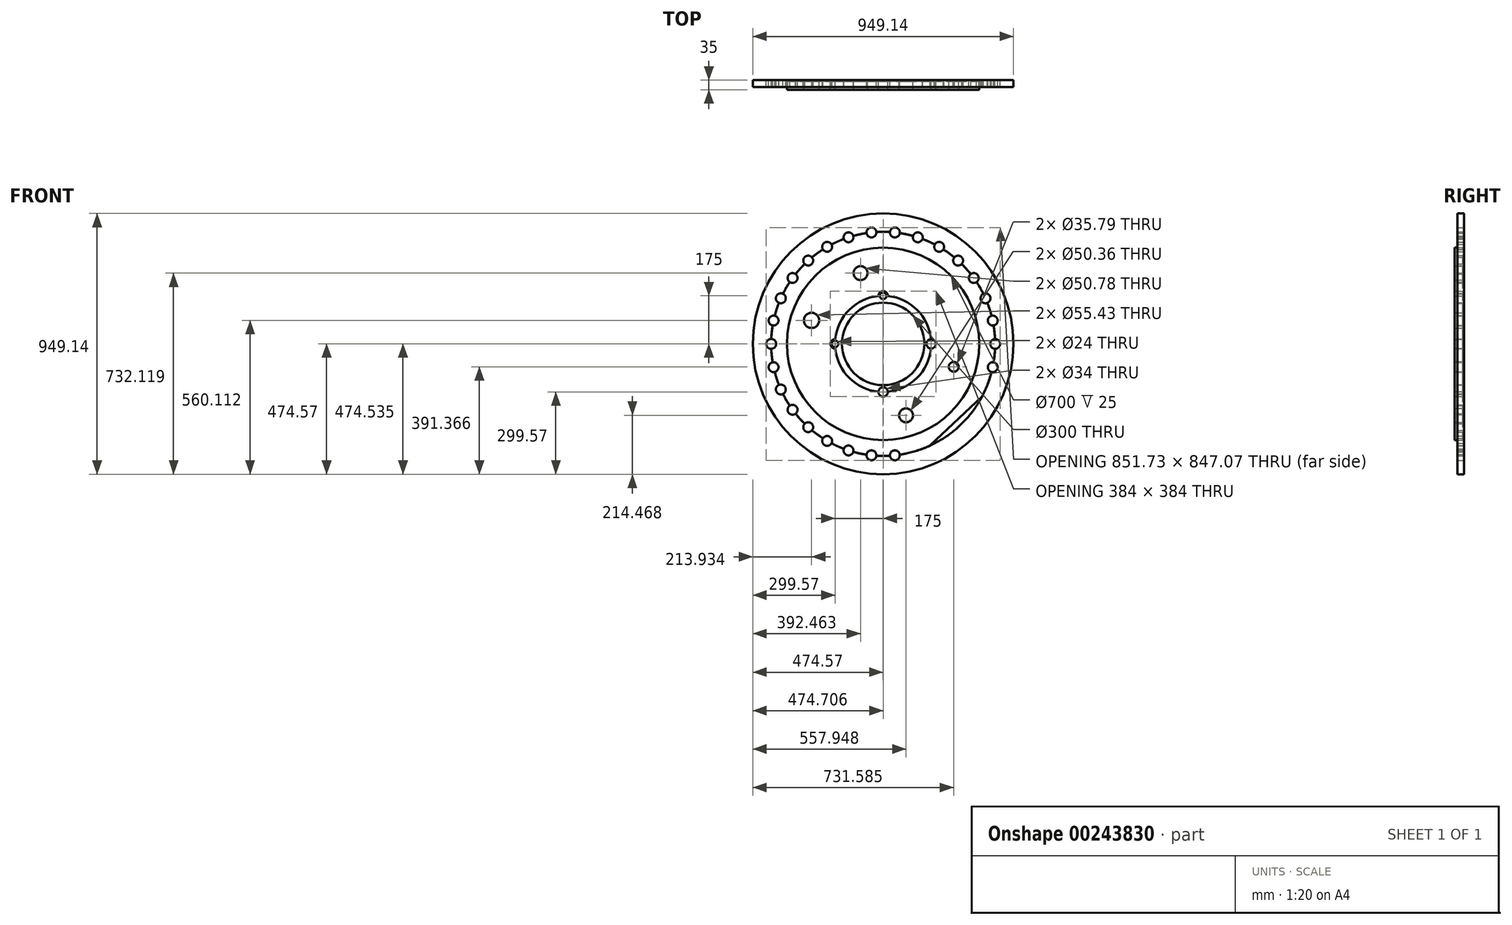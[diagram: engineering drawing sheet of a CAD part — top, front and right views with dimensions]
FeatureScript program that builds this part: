
annotation { "Feature Type Name" : "Feature", "Feature Type Description" : "" }
export const myFeature = defineFeature(function(context is Context, id is Id, definition is map)
    precondition{}
    {
        {
            var Q0;
            Q0=qCreatedBy(makeId("Front.planeOp"),FACE);
            var sketch = newSketch(context, id + "F0", { "sketchPlane" : qUnion([Q0])});
            skCircle(sketch, "E0", {"center": v(0, 0) * mm, "radius": 150 * mm});
            skCircle(sketch, "E1", {"center": v(0, 0) * mm, "radius": 175 * mm});
            skLineSegment(sketch, "E2", {"start": v(0, -200.12) * mm, "end": v(0, 224.8) * mm});
            skCircle(sketch, "E3", {"center": v(0, 175) * mm, "radius": 12 * mm});
            skCircle(sketch, "E4", {"center": v(-175, 0) * mm, "radius": 12 * mm});
            skCircle(sketch, "E5", {"center": v(175, 0) * mm, "radius": 12 * mm});
            skCircle(sketch, "E6", {"center": v(0, -175) * mm, "radius": 12 * mm});
            skCircle(sketch, "E7", {"center": v(0, 175) * mm, "radius": 17 * mm});
            skCircle(sketch, "E8", {"center": v(175, 0) * mm, "radius": 17 * mm});
            skCircle(sketch, "E9", {"center": v(0, -175) * mm, "radius": 17 * mm});
            skCircle(sketch, "E10", {"center": v(-175, 0) * mm, "radius": 17 * mm});
            skCircle(sketch, "E11", {"center": v(0, 0) * mm, "radius": 350 * mm});
            skCircle(sketch, "E12", {"center": v(0, 0) * mm, "radius": 474.57 * mm});
            skCircle(sketch, "E13", {"center": v(0, 0) * mm, "radius": 407.73 * mm});
            skCircle(sketch, "E14.1.0", {"center": v(-0.05, -0.03) * mm, "radius": 407.73 * mm});
            skCircle(sketch, "E14.2.0", {"center": v(0, -0.06) * mm, "radius": 407.73 * mm});
            skPoint(sketch, "E14.center", {"position": v(-0.02, -0.03) * mm});
            skCircle(sketch, "E15", {"center": v(-407.73, 0) * mm, "radius": 18 * mm});
            skCircle(sketch, "E16.1.0", {"center": v(-398.83, -84.8) * mm, "radius": 18 * mm});
            skCircle(sketch, "E16.1.1", {"center": v(0.01, -0.09) * mm, "radius": 407.73 * mm});
            skCircle(sketch, "E16.2.0", {"center": v(-372.48, -165.9) * mm, "radius": 18 * mm});
            skCircle(sketch, "E16.2.1", {"center": v(0.03, -0.11) * mm, "radius": 407.73 * mm});
            skCircle(sketch, "E16.3.0", {"center": v(-329.86, -239.74) * mm, "radius": 18 * mm});
            skCircle(sketch, "E16.3.1", {"center": v(0.04, -0.14) * mm, "radius": 407.73 * mm});
            skCircle(sketch, "E16.4.0", {"center": v(-272.8, -303.12) * mm, "radius": 18 * mm});
            skCircle(sketch, "E16.4.1", {"center": v(0.07, -0.15) * mm, "radius": 407.73 * mm});
            skCircle(sketch, "E16.5.0", {"center": v(-203.83, -353.24) * mm, "radius": 18 * mm});
            skCircle(sketch, "E16.5.1", {"center": v(0.1, -0.16) * mm, "radius": 407.73 * mm});
            skCircle(sketch, "E16.6.0", {"center": v(-125.94, -387.93) * mm, "radius": 18 * mm});
            skCircle(sketch, "E16.7.0", {"center": v(-42.53, -405.66) * mm, "radius": 18 * mm});
            skCircle(sketch, "E16.7.1", {"center": v(0.15, -0.17) * mm, "radius": 407.73 * mm});
            skCircle(sketch, "E16.8.0", {"center": v(42.73, -405.67) * mm, "radius": 18 * mm});
            skCircle(sketch, "E16.8.1", {"center": v(0.18, -0.16) * mm, "radius": 407.73 * mm});
            skCircle(sketch, "E16.9.1", {"center": v(0.2, -0.15) * mm, "radius": 407.73 * mm});
            skCircle(sketch, "E16.10.1", {"center": v(0.23, -0.14) * mm, "radius": 407.73 * mm});
            skCircle(sketch, "E16.11.1", {"center": v(0.25, -0.11) * mm, "radius": 407.73 * mm});
            skCircle(sketch, "E16.12.1", {"center": v(0.26, -0.1) * mm, "radius": 407.73 * mm});
            skCircle(sketch, "E16.13.1", {"center": v(0.27, -0.06) * mm, "radius": 407.73 * mm});
            skCircle(sketch, "E16.14.0", {"center": v(399.08, -84.87) * mm, "radius": 18 * mm});
            skCircle(sketch, "E16.14.1", {"center": v(0.27, -0.04) * mm, "radius": 407.73 * mm});
            skCircle(sketch, "E16.15.0", {"center": v(408, -0.07) * mm, "radius": 18 * mm});
            skCircle(sketch, "E16.15.1", {"center": v(0.27, 0) * mm, "radius": 407.73 * mm});
            skCircle(sketch, "E16.16.0", {"center": v(399.1, 84.73) * mm, "radius": 18 * mm});
            skCircle(sketch, "E16.16.1", {"center": v(0.26, 0.02) * mm, "radius": 407.73 * mm});
            skCircle(sketch, "E16.17.0", {"center": v(372.75, 165.83) * mm, "radius": 18 * mm});
            skCircle(sketch, "E16.18.0", {"center": v(330.13, 239.67) * mm, "radius": 18 * mm});
            skCircle(sketch, "E16.18.1", {"center": v(0.23, 0.07) * mm, "radius": 407.73 * mm});
            skCircle(sketch, "E16.19.0", {"center": v(273.08, 303.05) * mm, "radius": 18 * mm});
            skCircle(sketch, "E16.19.1", {"center": v(0.2, 0.08) * mm, "radius": 407.73 * mm});
            skCircle(sketch, "E16.20.0", {"center": v(204.1, 353.17) * mm, "radius": 18 * mm});
            skCircle(sketch, "E16.20.1", {"center": v(0.18, 0.1) * mm, "radius": 407.73 * mm});
            skCircle(sketch, "E16.21.0", {"center": v(126.2, 387.86) * mm, "radius": 18 * mm});
            skCircle(sketch, "E16.21.1", {"center": v(0.15, 0.1) * mm, "radius": 407.73 * mm});
            skCircle(sketch, "E16.22.0", {"center": v(42.8, 405.6) * mm, "radius": 18 * mm});
            skCircle(sketch, "E16.22.1", {"center": v(0.12, 0.1) * mm, "radius": 407.73 * mm});
            skCircle(sketch, "E16.23.0", {"center": v(-42.46, 405.6) * mm, "radius": 18 * mm});
            skCircle(sketch, "E16.23.1", {"center": v(0.1, 0.1) * mm, "radius": 407.73 * mm});
            skCircle(sketch, "E16.24.0", {"center": v(-125.87, 387.88) * mm, "radius": 18 * mm});
            skCircle(sketch, "E16.24.1", {"center": v(0.07, 0.08) * mm, "radius": 407.73 * mm});
            skCircle(sketch, "E16.25.0", {"center": v(-203.77, 353.2) * mm, "radius": 18 * mm});
            skCircle(sketch, "E16.25.1", {"center": v(0.05, 0.07) * mm, "radius": 407.73 * mm, "construction": true});
            skCircle(sketch, "E16.26.0", {"center": v(-272.75, 303.1) * mm, "radius": 18 * mm});
            skCircle(sketch, "E16.26.1", {"center": v(0.03, 0.05) * mm, "radius": 407.73 * mm});
            skCircle(sketch, "E16.27.0", {"center": v(-329.81, 239.73) * mm, "radius": 18 * mm});
            skCircle(sketch, "E16.27.1", {"center": v(0.01, 0.02) * mm, "radius": 407.73 * mm});
            skCircle(sketch, "E16.28.0", {"center": v(-372.45, 165.9) * mm, "radius": 18 * mm});
            skCircle(sketch, "E16.29.0", {"center": v(-398.81, 84.8) * mm, "radius": 18 * mm});
            skCircle(sketch, "E16.29.1", {"center": v(0, -0.03) * mm, "radius": 407.73 * mm});
            skPoint(sketch, "E16.center", {"position": v(0.14, -0.03) * mm});
            skLineSegment(sketch, "E17", {"start": v(138.72, -1170.66) * mm, "end": v(1275.05, -27.76) * mm});
            skCircle(sketch, "E18.MirrorC", {"center": v(1310.26, -1302.45) * mm, "radius": 407.73 * mm});
            skCircle(sketch, "E19.MirrorC", {"center": v(1310.23, -1302.58) * mm, "radius": 407.73 * mm});
            skCircle(sketch, "E20.MirrorC", {"center": v(1310.07, -1302.37) * mm, "radius": 407.73 * mm});
            skCircle(sketch, "E21.MirrorC", {"center": v(1310, -1302.56) * mm, "radius": 407.73 * mm});
            skCircle(sketch, "E22.MirrorC", {"center": v(1310.07, -1302.62) * mm, "radius": 407.73 * mm});
            skCircle(sketch, "E23.MirrorC", {"center": v(1310.16, -1302.62) * mm, "radius": 407.73 * mm});
            skCircle(sketch, "E24.MirrorC", {"center": v(1310, -1302.53) * mm, "radius": 407.73 * mm});
            skCircle(sketch, "E25.MirrorC", {"center": v(1310.2, -1302.38) * mm, "radius": 407.73 * mm});
            skCircle(sketch, "E26.MirrorC", {"center": v(1310.03, -1302.4) * mm, "radius": 407.73 * mm});
            skCircle(sketch, "E27.MirrorC", {"center": v(1310, -1302.42) * mm, "radius": 407.73 * mm});
            skCircle(sketch, "E28.MirrorC", {"center": v(1310.1, -1302.36) * mm, "radius": 407.73 * mm});
            skCircle(sketch, "E29.MirrorC", {"center": v(1310.26, -1302.48) * mm, "radius": 407.73 * mm});
            skCircle(sketch, "E30.MirrorC", {"center": v(1310.26, -1302.5) * mm, "radius": 407.73 * mm});
            skCircle(sketch, "E31.MirrorC", {"center": v(1310, -1302.5) * mm, "radius": 407.73 * mm});
            skCircle(sketch, "E32.MirrorC", {"center": v(1135.17, -1303.64) * mm, "radius": 17 * mm});
            skCircle(sketch, "E33.MirrorC", {"center": v(1310.16, -1302.63) * mm, "radius": 407.73 * mm});
            skCircle(sketch, "E34.MirrorC", {"center": v(1310.23, -1302.4) * mm, "radius": 407.73 * mm});
            skCircle(sketch, "E35.MirrorC", {"center": v(1310.13, -1302.63) * mm, "radius": 407.73 * mm});
            skCircle(sketch, "E36.MirrorC", {"center": v(1135.17, -1303.64) * mm, "radius": 12 * mm});
            skCircle(sketch, "E37.MirrorC", {"center": v(1485.16, -1301.62) * mm, "radius": 12 * mm});
            skCircle(sketch, "E38.MirrorC", {"center": v(1310.13, -1302.68) * mm, "radius": 407.73 * mm});
            skCircle(sketch, "E39.MirrorC", {"center": v(1485.16, -1301.62) * mm, "radius": 17 * mm});
            skCircle(sketch, "E40.MirrorC", {"center": v(1310.2, -1302.6) * mm, "radius": 407.73 * mm});
            skCircle(sketch, "E41.MirrorC", {"center": v(1310.05, -1302.6) * mm, "radius": 407.73 * mm});
            skCircle(sketch, "E42.MirrorC", {"center": v(1310.26, -1302.53) * mm, "radius": 407.73 * mm});
            skCircle(sketch, "E43.MirrorC", {"center": v(1310.13, -1302.36) * mm, "radius": 407.73 * mm});
            skCircle(sketch, "E44.MirrorC", {"center": v(1311.17, -1477.62) * mm, "radius": 12 * mm});
            skCircle(sketch, "E45.MirrorC", {"center": v(1309.15, -1127.63) * mm, "radius": 12 * mm});
            skCircle(sketch, "E46.MirrorC", {"center": v(1311.17, -1477.62) * mm, "radius": 17 * mm});
            skCircle(sketch, "E47.MirrorC", {"center": v(1309.15, -1127.63) * mm, "radius": 17 * mm});
            skCircle(sketch, "E48.MirrorC", {"center": v(1614.82, -1573.63) * mm, "radius": 18 * mm});
            skCircle(sketch, "E49.MirrorC", {"center": v(922.97, -1430.8) * mm, "radius": 18 * mm});
            skCircle(sketch, "E50.MirrorC", {"center": v(1662.15, -1096.5) * mm, "radius": 18 * mm});
            skCircle(sketch, "E51.MirrorC", {"center": v(1310.05, -1302.38) * mm, "radius": 407.73 * mm});
            skCircle(sketch, "E52.MirrorC", {"center": v(1310.24, -1302.42) * mm, "radius": 407.73 * mm});
            skCircle(sketch, "E53.MirrorC", {"center": v(955.72, -1100.63) * mm, "radius": 18 * mm});
            skCircle(sketch, "E54.MirrorC", {"center": v(1715.5, -1257.48) * mm, "radius": 18 * mm});
            skLineSegment(sketch, "E55.MirrorCS", {"start": v(1311.46, -1527.92) * mm, "end": v(1310.64, -1384.55) * mm});
            skCircle(sketch, "E56.MirrorC", {"center": v(1005.43, -1031.35) * mm, "radius": 18 * mm});
            skCircle(sketch, "E57.MirrorC", {"center": v(1072.32, -1633.86) * mm, "radius": 18 * mm});
            skCircle(sketch, "E58.MirrorC", {"center": v(1146.42, -1676.06) * mm, "radius": 18 * mm});
            skCircle(sketch, "E59.MirrorC", {"center": v(1310, -1302.48) * mm, "radius": 407.73 * mm});
            skPoint(sketch, "E60.MirrorP", {"position": v(1310.13, -1302.5) * mm});
            skCircle(sketch, "E61.MirrorC", {"center": v(1227.66, -1701.93) * mm, "radius": 18 * mm});
            skCircle(sketch, "E62.MirrorC", {"center": v(1473.84, -928.92) * mm, "radius": 18 * mm});
            skCircle(sketch, "E63.MirrorC", {"center": v(921.5, -1178.73) * mm, "radius": 18 * mm});
            skCircle(sketch, "E64.MirrorC", {"center": v(1310.1, -1302.62) * mm, "radius": 407.73 * mm});
            skCircle(sketch, "E65.MirrorC", {"center": v(1551.8, -1631.05) * mm, "radius": 18 * mm});
            skCircle(sketch, "E66.MirrorC", {"center": v(1312.51, -1710.35) * mm, "radius": 18 * mm});
            skCircle(sketch, "E67.MirrorC", {"center": v(1307.74, -894.63) * mm, "radius": 18 * mm});
            skCircle(sketch, "E68.MirrorC", {"center": v(1547.93, -971.12) * mm, "radius": 18 * mm});
            skCircle(sketch, "E69.MirrorC", {"center": v(1142.05, -930.86) * mm, "radius": 18 * mm});
            skCircle(sketch, "E70.MirrorC", {"center": v(1397.26, -1700.94) * mm, "radius": 18 * mm});
            skCircle(sketch, "E71.MirrorC", {"center": v(1664.54, -1504.35) * mm, "radius": 18 * mm});
            skCircle(sketch, "E72.MirrorC", {"center": v(958.1, -1508.49) * mm, "radius": 18 * mm});
            skCircle(sketch, "E73.MirrorC", {"center": v(904.25, -1262.23) * mm, "radius": 18 * mm});
            skCircle(sketch, "E74.MirrorC", {"center": v(1223, -904.04) * mm, "radius": 18 * mm});
            skCircle(sketch, "E75.MirrorC", {"center": v(1698.76, -1426.26) * mm, "radius": 18 * mm});
            skCircle(sketch, "E76.MirrorC", {"center": v(1310.03, -1302.58) * mm, "radius": 407.73 * mm});
            skCircle(sketch, "E77.MirrorC", {"center": v(904.75, -1347.5) * mm, "radius": 18 * mm});
            skCircle(sketch, "E78.MirrorC", {"center": v(1392.6, -903.05) * mm, "radius": 18 * mm});
            skCircle(sketch, "E79.MirrorC", {"center": v(1008.63, -1577.18) * mm, "radius": 18 * mm});
            skCircle(sketch, "E80.MirrorC", {"center": v(1611.63, -1027.8) * mm, "radius": 18 * mm});
            skCircle(sketch, "E81.MirrorC", {"center": v(1478.2, -1674.12) * mm, "radius": 18 * mm});
            skCircle(sketch, "E82.MirrorC", {"center": v(1697.29, -1174.18) * mm, "radius": 18 * mm});
            skCircle(sketch, "E83.MirrorC", {"center": v(1068.46, -973.93) * mm, "radius": 18 * mm});
            skCircle(sketch, "E84.MirrorC", {"center": v(1716, -1342.75) * mm, "radius": 18 * mm});
            skCircle(sketch, "E85.MirrorC", {"center": v(1310.16, -1302.63) * mm, "radius": 175 * mm});
            skCircle(sketch, "E86.MirrorC", {"center": v(1310.18, -1302.61) * mm, "radius": 407.73 * mm});
            skLineSegment(sketch, "E87.MirrorCS", {"start": v(1110.04, -1303.78) * mm, "end": v(1534.96, -1301.33) * mm});
            skCircle(sketch, "E88.MirrorC", {"center": v(1310.16, -1302.63) * mm, "radius": 474.57 * mm});
            skPoint(sketch, "E89.MirrorP", {"position": v(1310.13, -1302.64) * mm});
            skCircle(sketch, "E90.MirrorC", {"center": v(1310, -1302.45) * mm, "radius": 407.73 * mm});
            skCircle(sketch, "E91.MirrorC", {"center": v(1310.18, -1302.37) * mm, "radius": 407.73 * mm});
            skLineSegment(sketch, "E92.MirrorCS", {"start": v(1313.31, -1848.69) * mm, "end": v(1306.73, -707.3) * mm});
            skCircle(sketch, "E93.MirrorC", {"center": v(1310.24, -1302.56) * mm, "radius": 407.73 * mm});
            skCircle(sketch, "E94.MirrorC", {"center": v(1310.16, -1302.63) * mm, "radius": 150 * mm});
            skCircle(sketch, "E95.MirrorC", {"center": v(1310.15, -1302.36) * mm, "radius": 407.73 * mm});
            skCircle(sketch, "E96.MirrorC", {"center": v(1310.16, -1302.63) * mm, "radius": 350 * mm});
            skLineSegment(sketch, "E97", {"start": v(-1444, -486.77) * mm, "end": v(749.23, -2667.38) * mm});
            skCircle(sketch, "E98.MirrorC", {"center": v(-1922.5, -1933.6) * mm, "radius": 407.73 * mm});
            skCircle(sketch, "E99.MirrorC", {"center": v(-612.36, -3236.01) * mm, "radius": 407.73 * mm});
            skCircle(sketch, "E100.MirrorC", {"center": v(-612.5, -3236.04) * mm, "radius": 407.73 * mm});
            skCircle(sketch, "E101.MirrorC", {"center": v(-1922.3, -1933.78) * mm, "radius": 407.73 * mm});
            skCircle(sketch, "E102.MirrorC", {"center": v(-1922.52, -1933.73) * mm, "radius": 407.73 * mm});
            skCircle(sketch, "E103.MirrorC", {"center": v(-1922.5, -1933.78) * mm, "radius": 407.73 * mm});
            skCircle(sketch, "E104.MirrorC", {"center": v(-612.54, -3236.14) * mm, "radius": 407.73 * mm});
            skCircle(sketch, "E105.MirrorC", {"center": v(-612.3, -3236.22) * mm, "radius": 407.73 * mm});
            skCircle(sketch, "E106.MirrorC", {"center": v(-1922.28, -1933.75) * mm, "radius": 407.73 * mm});
            skCircle(sketch, "E107.MirrorC", {"center": v(-1922.47, -1933.8) * mm, "radius": 407.73 * mm});
            skCircle(sketch, "E108.MirrorC", {"center": v(-1922.34, -1933.56) * mm, "radius": 407.73 * mm});
            skCircle(sketch, "E109.MirrorC", {"center": v(-612.54, -3236.17) * mm, "radius": 407.73 * mm});
            skCircle(sketch, "E110.MirrorC", {"center": v(-612.27, -3236.17) * mm, "radius": 407.73 * mm});
            skCircle(sketch, "E111.MirrorC", {"center": v(-612.51, -3236.22) * mm, "radius": 407.73 * mm});
            skCircle(sketch, "E112.MirrorC", {"center": v(-1922.27, -1933.64) * mm, "radius": 407.73 * mm});
            skCircle(sketch, "E113.MirrorC", {"center": v(-612.3, -3236.06) * mm, "radius": 407.73 * mm});
            skCircle(sketch, "E114.MirrorC", {"center": v(-1922.3, -1933.6) * mm, "radius": 407.73 * mm});
            skCircle(sketch, "E115.MirrorC", {"center": v(-1922.32, -1933.58) * mm, "radius": 407.73 * mm});
            skCircle(sketch, "E116.MirrorC", {"center": v(-1922.48, -1933.58) * mm, "radius": 407.73 * mm});
            skCircle(sketch, "E117.MirrorC", {"center": v(-612.47, -3236.03) * mm, "radius": 407.73 * mm});
            skCircle(sketch, "E118.MirrorC", {"center": v(-612.45, -3236.01) * mm, "radius": 407.73 * mm});
            skCircle(sketch, "E119.MirrorC", {"center": v(-612.53, -3236.2) * mm, "radius": 407.73 * mm});
            skCircle(sketch, "E120.MirrorC", {"center": v(-1922.51, -1933.76) * mm, "radius": 407.73 * mm});
            skCircle(sketch, "E121.MirrorC", {"center": v(-612.27, -3236.12) * mm, "radius": 407.73 * mm});
            skCircle(sketch, "E122.MirrorC", {"center": v(-1922.31, -1933.8) * mm, "radius": 407.73 * mm});
            skCircle(sketch, "E123.MirrorC", {"center": v(-1922.28, -1933.62) * mm, "radius": 407.73 * mm});
            skCircle(sketch, "E124.MirrorC", {"center": v(-1922.42, -1933.55) * mm, "radius": 407.73 * mm});
            skCircle(sketch, "E125.MirrorC", {"center": v(-1922.45, -1933.56) * mm, "radius": 407.73 * mm});
            skCircle(sketch, "E126.MirrorC", {"center": v(-612.34, -3236.26) * mm, "radius": 407.73 * mm});
            skCircle(sketch, "E127.MirrorC", {"center": v(-612.36, -3236.27) * mm, "radius": 407.73 * mm});
            skCircle(sketch, "E128.MirrorC", {"center": v(-612.42, -3236.28) * mm, "radius": 407.73 * mm});
            skCircle(sketch, "E129.MirrorC", {"center": v(-1922.43, -1933.55) * mm, "radius": 407.73 * mm});
            skCircle(sketch, "E130.MirrorC", {"center": v(-612.42, -3236) * mm, "radius": 407.73 * mm});
            skCircle(sketch, "E131.MirrorC", {"center": v(-612.27, -3236.18) * mm, "radius": 407.73 * mm});
            skCircle(sketch, "E132.MirrorC", {"center": v(-1921.42, -2108.55) * mm, "radius": 12 * mm});
            skCircle(sketch, "E133.MirrorC", {"center": v(-612.39, -3236.28) * mm, "radius": 407.73 * mm});
            skCircle(sketch, "E134.MirrorC", {"center": v(-2097.43, -1934.56) * mm, "radius": 12 * mm});
            skCircle(sketch, "E135.MirrorC", {"center": v(-612.27, -3236.14) * mm, "radius": 407.73 * mm});
            skCircle(sketch, "E136.MirrorC", {"center": v(-1922.4, -1933.55) * mm, "radius": 407.73 * mm});
            skCircle(sketch, "E137.MirrorC", {"center": v(-1922.4, -1933.5) * mm, "radius": 407.73 * mm});
            skCircle(sketch, "E138.MirrorC", {"center": v(-437.27, -3236.18) * mm, "radius": 12 * mm});
            skCircle(sketch, "E139.MirrorC", {"center": v(-612.39, -3236) * mm, "radius": 407.73 * mm});
            skCircle(sketch, "E140.MirrorC", {"center": v(-1921.42, -2108.55) * mm, "radius": 17 * mm});
            skCircle(sketch, "E141.MirrorC", {"center": v(-1922.37, -1933.82) * mm, "radius": 407.73 * mm});
            skCircle(sketch, "E142.MirrorC", {"center": v(-612.31, -3236.04) * mm, "radius": 407.73 * mm});
            skCircle(sketch, "E143.MirrorC", {"center": v(-1922.53, -1933.7) * mm, "radius": 407.73 * mm});
            skCircle(sketch, "E144.MirrorC", {"center": v(-1922.34, -1933.81) * mm, "radius": 407.73 * mm});
            skCircle(sketch, "E145.MirrorC", {"center": v(-612.45, -3236.27) * mm, "radius": 407.73 * mm});
            skCircle(sketch, "E146.MirrorC", {"center": v(-2097.43, -1934.56) * mm, "radius": 17 * mm});
            skCircle(sketch, "E147.MirrorC", {"center": v(-1747.43, -1932.54) * mm, "radius": 17 * mm});
            skCircle(sketch, "E148.MirrorC", {"center": v(-1923.44, -1758.55) * mm, "radius": 12 * mm});
            skCircle(sketch, "E149.MirrorC", {"center": v(-437.27, -3236.18) * mm, "radius": 17 * mm});
            skCircle(sketch, "E150.MirrorC", {"center": v(-1923.44, -1758.55) * mm, "radius": 17 * mm});
            skCircle(sketch, "E151.MirrorC", {"center": v(-1922.53, -1933.67) * mm, "radius": 407.73 * mm});
            skCircle(sketch, "E152.MirrorC", {"center": v(-1922.37, -1933.55) * mm, "radius": 407.73 * mm});
            skCircle(sketch, "E153.MirrorC", {"center": v(-1922.26, -1933.67) * mm, "radius": 407.73 * mm});
            skCircle(sketch, "E154.MirrorC", {"center": v(-612.27, -3061.18) * mm, "radius": 17 * mm});
            skCircle(sketch, "E155.MirrorC", {"center": v(-612.51, -3236.06) * mm, "radius": 407.73 * mm});
            skCircle(sketch, "E156.MirrorC", {"center": v(-612.53, -3236.09) * mm, "radius": 407.73 * mm});
            skCircle(sketch, "E157.MirrorC", {"center": v(-612.27, -3411.18) * mm, "radius": 12 * mm});
            skCircle(sketch, "E158.MirrorC", {"center": v(-612.27, -3061.18) * mm, "radius": 12 * mm});
            skCircle(sketch, "E159.MirrorC", {"center": v(-1747.43, -1932.54) * mm, "radius": 12 * mm});
            skCircle(sketch, "E160.MirrorC", {"center": v(-1922.52, -1933.65) * mm, "radius": 407.73 * mm});
            skCircle(sketch, "E161.MirrorC", {"center": v(-787.27, -3236.18) * mm, "radius": 17 * mm});
            skCircle(sketch, "E162.MirrorC", {"center": v(-612.47, -3236.26) * mm, "radius": 407.73 * mm});
            skCircle(sketch, "E163.MirrorC", {"center": v(-612.31, -3236.24) * mm, "radius": 407.73 * mm});
            skCircle(sketch, "E164.MirrorC", {"center": v(-612.27, -3411.18) * mm, "radius": 17 * mm});
            skCircle(sketch, "E165.MirrorC", {"center": v(-1922.4, -1933.82) * mm, "radius": 407.73 * mm});
            skCircle(sketch, "E166.MirrorC", {"center": v(-612.54, -3236.12) * mm, "radius": 407.73 * mm});
            skCircle(sketch, "E167.MirrorC", {"center": v(-787.27, -3236.18) * mm, "radius": 12 * mm});
            skCircle(sketch, "E168.MirrorC", {"center": v(-282.41, -2996.43) * mm, "radius": 18 * mm});
            skCircle(sketch, "E169.MirrorC", {"center": v(-213.44, -3151.38) * mm, "radius": 18 * mm});
            skCircle(sketch, "E170.MirrorC", {"center": v(-1535.24, -1805.38) * mm, "radius": 18 * mm});
            skCircle(sketch, "E171.MirrorC", {"center": v(-239.78, -3070.28) * mm, "radius": 18 * mm});
            skCircle(sketch, "E172.MirrorC", {"center": v(-2327.77, -1978.7) * mm, "radius": 18 * mm});
            skCircle(sketch, "E173.MirrorC", {"center": v(-942.35, -2996.38) * mm, "radius": 18 * mm});
            skCircle(sketch, "E174.MirrorC", {"center": v(-738.4, -2848.23) * mm, "radius": 18 * mm});
            skPoint(sketch, "E175.MirrorP", {"position": v(-1922.4, -1933.69) * mm});
            skCircle(sketch, "E176.MirrorC", {"center": v(-339.46, -2933.06) * mm, "radius": 18 * mm});
            skCircle(sketch, "E177.MirrorC", {"center": v(-1920, -2341.55) * mm, "radius": 18 * mm});
            skCircle(sketch, "E178.MirrorC", {"center": v(-339.51, -3539.27) * mm, "radius": 18 * mm});
            skCircle(sketch, "E179.MirrorC", {"center": v(-942.4, -3475.85) * mm, "radius": 18 * mm});
            skCircle(sketch, "E180.MirrorC", {"center": v(-1517.02, -1888.68) * mm, "radius": 18 * mm});
            skCircle(sketch, "E181.MirrorC", {"center": v(-1922.42, -1933.82) * mm, "radius": 407.73 * mm});
            skCircle(sketch, "E182.MirrorC", {"center": v(-1922.26, -1933.7) * mm, "radius": 407.73 * mm});
            skCircle(sketch, "E183.MirrorC", {"center": v(-1922.45, -1933.81) * mm, "radius": 407.73 * mm});
            skCircle(sketch, "E184.MirrorC", {"center": v(-1758.68, -1560.12) * mm, "radius": 18 * mm});
            skCircle(sketch, "E185.MirrorC", {"center": v(-1570.37, -1727.69) * mm, "radius": 18 * mm});
            skCircle(sketch, "E186.MirrorC", {"center": v(-985, -3070.22) * mm, "radius": 18 * mm});
            skCircle(sketch, "E187.MirrorC", {"center": v(-2227.1, -1662.55) * mm, "radius": 18 * mm});
            skCircle(sketch, "E188.MirrorC", {"center": v(-2160.2, -2265.06) * mm, "radius": 18 * mm});
            skCircle(sketch, "E189.MirrorC", {"center": v(-1567.98, -2135.55) * mm, "radius": 18 * mm});
            skCircle(sketch, "E190.MirrorC", {"center": v(-1922.51, -1933.62) * mm, "radius": 407.73 * mm});
            skCircle(sketch, "E191.MirrorC", {"center": v(-1011.35, -3151.3) * mm, "radius": 18 * mm});
            skCircle(sketch, "E192.MirrorC", {"center": v(-738.47, -3624.04) * mm, "radius": 18 * mm});
            skCircle(sketch, "E193.MirrorC", {"center": v(-612.21, -3236.14) * mm, "radius": 407.73 * mm});
            skCircle(sketch, "E194.MirrorC", {"center": v(-612.5, -3236.24) * mm, "radius": 407.73 * mm});
            skCircle(sketch, "E195.MirrorC", {"center": v(-239.81, -3402.07) * mm, "radius": 18 * mm});
            skCircle(sketch, "E196.MirrorC", {"center": v(-2009.53, -1535.24) * mm, "radius": 18 * mm});
            skCircle(sketch, "E197.MirrorC", {"center": v(-816.3, -2882.9) * mm, "radius": 18 * mm});
            skCircle(sketch, "E198.MirrorC", {"center": v(-486.4, -3624.06) * mm, "radius": 18 * mm});
            skCircle(sketch, "E199.MirrorC", {"center": v(-1835.26, -2332.14) * mm, "radius": 18 * mm});
            skCircle(sketch, "E200.MirrorC", {"center": v(-569.8, -3641.78) * mm, "radius": 18 * mm});
            skCircle(sketch, "E201.MirrorC", {"center": v(-213.46, -3320.98) * mm, "radius": 18 * mm});
            skCircle(sketch, "E202.MirrorC", {"center": v(-1754.32, -2305.31) * mm, "radius": 18 * mm});
            skCircle(sketch, "E203.MirrorC", {"center": v(-2090.47, -1562.06) * mm, "radius": 18 * mm});
            skCircle(sketch, "E204.MirrorC", {"center": v(-816.37, -3589.35) * mm, "radius": 18 * mm});
            skCircle(sketch, "E205.MirrorC", {"center": v(-1011.36, -3320.9) * mm, "radius": 18 * mm});
            skCircle(sketch, "E206.MirrorC", {"center": v(-885.3, -2933.02) * mm, "radius": 18 * mm});
            skCircle(sketch, "E207.MirrorC", {"center": v(-655, -2830.5) * mm, "radius": 18 * mm});
            skCircle(sketch, "E208.MirrorC", {"center": v(-408.5, -3589.38) * mm, "radius": 18 * mm});
            skCircle(sketch, "E209.MirrorC", {"center": v(-612.28, -3236.2) * mm, "radius": 407.73 * mm});
            skCircle(sketch, "E210.MirrorC", {"center": v(-2004.86, -2333.13) * mm, "radius": 18 * mm});
            skCircle(sketch, "E211.MirrorC", {"center": v(-885.35, -3539.22) * mm, "radius": 18 * mm});
            skCircle(sketch, "E212.MirrorC", {"center": v(-1924.78, -1525.83) * mm, "radius": 18 * mm});
            skCircle(sketch, "E213.MirrorC", {"center": v(-1516.52, -1973.95) * mm, "radius": 18 * mm});
            skCircle(sketch, "E214.MirrorC", {"center": v(-1922.27, -1933.73) * mm, "radius": 407.73 * mm});
            skCircle(sketch, "E215.MirrorC", {"center": v(-985.02, -3402) * mm, "radius": 18 * mm});
            skCircle(sketch, "E216.MirrorC", {"center": v(-1680.73, -2262.25) * mm, "radius": 18 * mm});
            skCircle(sketch, "E217.MirrorC", {"center": v(-2274.42, -2139.68) * mm, "radius": 18 * mm});
            skCircle(sketch, "E218.MirrorC", {"center": v(-408.44, -2882.94) * mm, "radius": 18 * mm});
            skCircle(sketch, "E219.MirrorC", {"center": v(-1533.76, -2057.45) * mm, "radius": 18 * mm});
            skLineSegment(sketch, "E220.MirrorCS", {"start": v(-1923.73, -1708.26) * mm, "end": v(-1922.9, -1851.63) * mm});
            skCircle(sketch, "E221.MirrorC", {"center": v(-612.34, -3236.03) * mm, "radius": 407.73 * mm});
            skCircle(sketch, "E222.MirrorC", {"center": v(-1684.6, -1602.32) * mm, "radius": 18 * mm});
            skCircle(sketch, "E223.MirrorC", {"center": v(-1617.7, -2204.82) * mm, "radius": 18 * mm});
            skCircle(sketch, "E224.MirrorC", {"center": v(-486.33, -2848.25) * mm, "radius": 18 * mm});
            skCircle(sketch, "E225.MirrorC", {"center": v(-612.28, -3236.09) * mm, "radius": 407.73 * mm});
            skCircle(sketch, "E226.MirrorC", {"center": v(-1020.27, -3236.1) * mm, "radius": 18 * mm});
            skCircle(sketch, "E227.MirrorC", {"center": v(-2309.55, -2062) * mm, "radius": 18 * mm});
            skCircle(sketch, "E228.MirrorC", {"center": v(-2164.06, -1605.13) * mm, "radius": 18 * mm});
            skCircle(sketch, "E229.MirrorC", {"center": v(-2223.9, -2208.37) * mm, "radius": 18 * mm});
            skCircle(sketch, "E230.MirrorC", {"center": v(-2086.1, -2307.26) * mm, "radius": 18 * mm});
            skCircle(sketch, "E231.MirrorC", {"center": v(-2276.8, -1731.83) * mm, "radius": 18 * mm});
            skCircle(sketch, "E232.MirrorC", {"center": v(-282.45, -3475.9) * mm, "radius": 18 * mm});
            skCircle(sketch, "E233.MirrorC", {"center": v(-2328.27, -1893.43) * mm, "radius": 18 * mm});
            skCircle(sketch, "E234.MirrorC", {"center": v(-1839.93, -1534.24) * mm, "radius": 18 * mm});
            skCircle(sketch, "E235.MirrorC", {"center": v(-2311.03, -1809.92) * mm, "radius": 18 * mm});
            skCircle(sketch, "E236.MirrorC", {"center": v(-569.73, -2830.52) * mm, "radius": 18 * mm});
            skLineSegment(sketch, "E237.MirrorCS", {"start": v(-386.97, -3236.18) * mm, "end": v(-530.35, -3236.18) * mm});
            skCircle(sketch, "E238.MirrorC", {"center": v(-204.54, -3236.18) * mm, "radius": 18 * mm});
            skPoint(sketch, "E239.MirrorP", {"position": v(-612.4, -3236.14) * mm});
            skCircle(sketch, "E240.MirrorC", {"center": v(-1620.9, -1659) * mm, "radius": 18 * mm});
            skCircle(sketch, "E241.MirrorC", {"center": v(-655.07, -3641.77) * mm, "radius": 18 * mm});
            skCircle(sketch, "E242.MirrorC", {"center": v(-612.27, -3236.18) * mm, "radius": 175 * mm});
            skCircle(sketch, "E243.MirrorC", {"center": v(-1922.43, -1933.55) * mm, "radius": 350 * mm});
            skCircle(sketch, "E244.MirrorC", {"center": v(-612.27, -3236.18) * mm, "radius": 350 * mm});
            skLineSegment(sketch, "E245.MirrorCS", {"start": v(-1925.58, -1387.5) * mm, "end": v(-1919, -2528.89) * mm});
            skPoint(sketch, "E246.MirrorP", {"position": v(-1922.4, -1933.54) * mm});
            skLineSegment(sketch, "E247.MirrorCS", {"start": v(-66.2, -3236.18) * mm, "end": v(-1207.61, -3236.18) * mm});
            skCircle(sketch, "E248.MirrorC", {"center": v(-1922.43, -1933.55) * mm, "radius": 150 * mm});
            skLineSegment(sketch, "E249.MirrorCS", {"start": v(-1722.3, -1932.4) * mm, "end": v(-2147.22, -1934.85) * mm});
            skCircle(sketch, "E250.MirrorC", {"center": v(-1922.43, -1933.55) * mm, "radius": 474.57 * mm});
            skCircle(sketch, "E251.MirrorC", {"center": v(-1922.43, -1933.55) * mm, "radius": 175 * mm});
            skLineSegment(sketch, "E252.MirrorCS", {"start": v(-750.99, -2065.52) * mm, "end": v(-1887.32, -3208.42) * mm});
            skCircle(sketch, "E253.MirrorC", {"center": v(-612.27, -3236.18) * mm, "radius": 474.57 * mm});
            skCircle(sketch, "E254.MirrorC", {"center": v(-612.27, -3236.18) * mm, "radius": 150 * mm});
            skPoint(sketch, "E255.MirrorP", {"position": v(-612.25, -3236.15) * mm});
            skLineSegment(sketch, "E256.MirrorCS", {"start": v(-612.27, -3036.05) * mm, "end": v(-612.27, -3460.98) * mm});
            skLineSegment(sketch, "E257", {"start": v(-1922.5, -1933.6) * mm, "end": v(-2288.93, -1577.32) * mm});
            skCircle(sketch, "E258", {"center": v(-2105.71, -1755.46) * mm, "radius": 25 * mm});
            skLineSegment(sketch, "E259", {"start": v(-1595.1, -2277.17) * mm, "end": v(-1536.48, -2335.86) * mm});
            skLineSegment(sketch, "E260", {"start": v(-1536.48, -2335.86) * mm, "end": v(-1510.29, -2309.7) * mm});
            skLineSegment(sketch, "E261", {"start": v(-1510.29, -2309.7) * mm, "end": v(-1569.31, -2250.61) * mm});
            skCircle(sketch, "E262", {"center": v(-260.64, 85.54) * mm, "radius": 27.72 * mm});
            skCircle(sketch, "E263", {"center": v(-82.1, 257.55) * mm, "radius": 25.39 * mm});
            skCircle(sketch, "E264", {"center": v(83.38, -260.1) * mm, "radius": 25.18 * mm});
            skCircle(sketch, "E265", {"center": v(257.02, -83.2) * mm, "radius": 17.9 * mm});
            skLineSegment(sketch, "E266", {"start": v(65.76, -469.63) * mm, "end": v(465.57, -91.98) * mm});
            skCircle(sketch, "E267", {"center": v(-2078.2, 846.23) * mm, "radius": 135.12 * mm});
            skSolve(sketch);
        }
        {
            var Q0;
            {var subQ0=sQuery(id+"F0.wireOp",EDGE,"E2");var subQ1=sQuery(id+"F0.wireOp",EDGE,"E0");var subQ2=makeQuery(id+"F0.imprint","INTERSECT",VERTEX,{"disambiguationData":[OD(0.0)],"derivedFrom":[subQ1,subQ0]});Q0=makeQuery(id+"F0.imprint","IMPRINT",FACE,{"disambiguationData":[TD([[makeQuery(id+"F0.imprint","IMPRINT",EDGE,{"disambiguationData":[TD([[subQ2,-1.0]])],"derivedFrom":subQ1}),-1.0]])]});}
            var Q1;
            {var subQ0=sQuery(id+"F0.wireOp",EDGE,"E10");var subQ1=sQuery(id+"F0.wireOp",EDGE,"E1");var subQ2=makeQuery(id+"F0.imprint","INTERSECT",VERTEX,{"disambiguationData":[OD(0.0)],"derivedFrom":[subQ1,subQ0]});Q1=makeQuery(id+"F0.imprint","IMPRINT",FACE,{"disambiguationData":[TD([[makeQuery(id+"F0.imprint","IMPRINT",EDGE,{"disambiguationData":[TD([[subQ2,-1.0]])],"derivedFrom":subQ1}),1.0]])]});}
            var Q2;
            {var subQ0=sQuery(id+"F0.wireOp",EDGE,"E10");var subQ1=sQuery(id+"F0.wireOp",EDGE,"E1");var subQ2=makeQuery(id+"F0.imprint","INTERSECT",VERTEX,{"disambiguationData":[OD(0.0)],"derivedFrom":[subQ1,subQ0]});Q2=makeQuery(id+"F0.imprint","IMPRINT",FACE,{"disambiguationData":[TD([[makeQuery(id+"F0.imprint","IMPRINT",EDGE,{"disambiguationData":[TD([[subQ2,-1.0]])],"derivedFrom":subQ1}),-1.0]])]});}
            var Q3;
            {var subQ0=sQuery(id+"F0.wireOp",EDGE,"E10");var subQ1=sQuery(id+"F0.wireOp",EDGE,"E1");var subQ2=makeQuery(id+"F0.imprint","INTERSECT",VERTEX,{"disambiguationData":[OD(1.0)],"derivedFrom":[subQ1,subQ0]});Q3=makeQuery(id+"F0.imprint","IMPRINT",FACE,{"disambiguationData":[TD([[makeQuery(id+"F0.imprint","IMPRINT",EDGE,{"disambiguationData":[TD([[subQ2,1.0]])],"derivedFrom":subQ1}),-1.0]])]});}
            var Q4;
            {var subQ0=sQuery(id+"F0.wireOp",EDGE,"E10");var subQ1=sQuery(id+"F0.wireOp",EDGE,"E1");var subQ2=makeQuery(id+"F0.imprint","INTERSECT",VERTEX,{"disambiguationData":[OD(1.0)],"derivedFrom":[subQ1,subQ0]});Q4=makeQuery(id+"F0.imprint","IMPRINT",FACE,{"disambiguationData":[TD([[makeQuery(id+"F0.imprint","IMPRINT",EDGE,{"disambiguationData":[TD([[subQ2,1.0]])],"derivedFrom":subQ1}),1.0]])]});}
            var Q5;
            {var subQ0=sQuery(id+"F0.wireOp",EDGE,"NZMgdJby-8j4q-fpOx-I2TN-UBzTeOVD87fY");var subQ1=sQuery(id+"F0.wireOp",EDGE,"E0");var subQ2=makeQuery(id+"F0.imprint","INTERSECT",VERTEX,{"disambiguationData":[OD(1.0)],"derivedFrom":[subQ1,subQ0]});Q5=makeQuery(id+"F0.imprint","IMPRINT",FACE,{"disambiguationData":[TD([[makeQuery(id+"F0.imprint","IMPRINT",EDGE,{"disambiguationData":[TD([[subQ2,-1.0]])],"derivedFrom":subQ1}),-1.0]])]});}
            var Q6;
            {var subQ0=sQuery(id+"F0.wireOp",EDGE,"E7");var subQ1=sQuery(id+"F0.wireOp",EDGE,"E1");var subQ2=makeQuery(id+"F0.imprint","INTERSECT",VERTEX,{"disambiguationData":[OD(1.0)],"derivedFrom":[subQ1,subQ0]});Q6=makeQuery(id+"F0.imprint","IMPRINT",FACE,{"disambiguationData":[TD([[makeQuery(id+"F0.imprint","IMPRINT",EDGE,{"disambiguationData":[TD([[subQ2,1.0]])],"derivedFrom":subQ1}),1.0]])]});}
            var Q7;
            {var subQ0=sQuery(id+"F0.wireOp",EDGE,"E7");var subQ1=sQuery(id+"F0.wireOp",EDGE,"E1");var subQ2=makeQuery(id+"F0.imprint","INTERSECT",VERTEX,{"disambiguationData":[OD(0.0)],"derivedFrom":[subQ1,subQ0]});Q7=makeQuery(id+"F0.imprint","IMPRINT",FACE,{"disambiguationData":[TD([[makeQuery(id+"F0.imprint","IMPRINT",EDGE,{"disambiguationData":[TD([[subQ2,-1.0]])],"derivedFrom":subQ1}),1.0]])]});}
            var Q8;
            {var subQ1=sQuery(id+"F0.wireOp",EDGE,"E0");var subQ5=sQuery(id+"F0.wireOp",EDGE,"E2");var subQ6=makeQuery(id+"F0.imprint","INTERSECT",VERTEX,{"disambiguationData":[OD(0.0)],"derivedFrom":[subQ1,subQ5]});Q8=makeQuery(id+"F0.imprint","IMPRINT",FACE,{"disambiguationData":[TD([[makeQuery(id+"F0.imprint","IMPRINT",EDGE,{"disambiguationData":[TD([[subQ6,1.0]])],"derivedFrom":subQ1}),-1.0]])]});}
            var Q9;
            {var subQ0=sQuery(id+"F0.wireOp",EDGE,"E7");var subQ1=sQuery(id+"F0.wireOp",EDGE,"E1");var subQ2=makeQuery(id+"F0.imprint","INTERSECT",VERTEX,{"disambiguationData":[OD(0.0)],"derivedFrom":[subQ1,subQ0]});Q9=makeQuery(id+"F0.imprint","IMPRINT",FACE,{"disambiguationData":[TD([[makeQuery(id+"F0.imprint","IMPRINT",EDGE,{"disambiguationData":[TD([[subQ2,-1.0]])],"derivedFrom":subQ1}),-1.0]])]});}
            var Q10;
            {var subQ0=sQuery(id+"F0.wireOp",EDGE,"E7");var subQ1=sQuery(id+"F0.wireOp",EDGE,"E1");var subQ2=makeQuery(id+"F0.imprint","INTERSECT",VERTEX,{"disambiguationData":[OD(1.0)],"derivedFrom":[subQ1,subQ0]});Q10=makeQuery(id+"F0.imprint","IMPRINT",FACE,{"disambiguationData":[TD([[makeQuery(id+"F0.imprint","IMPRINT",EDGE,{"disambiguationData":[TD([[subQ2,1.0]])],"derivedFrom":subQ1}),-1.0]])]});}
            var Q11;
            {var subQ0=sQuery(id+"F0.wireOp",EDGE,"E8");var subQ1=sQuery(id+"F0.wireOp",EDGE,"E1");var subQ2=makeQuery(id+"F0.imprint","INTERSECT",VERTEX,{"disambiguationData":[OD(0.0)],"derivedFrom":[subQ1,subQ0]});Q11=makeQuery(id+"F0.imprint","IMPRINT",FACE,{"disambiguationData":[TD([[makeQuery(id+"F0.imprint","IMPRINT",EDGE,{"disambiguationData":[TD([[subQ2,1.0]])],"derivedFrom":subQ1}),-1.0]])]});}
            var Q12;
            {var subQ0=sQuery(id+"F0.wireOp",EDGE,"E8");var subQ1=sQuery(id+"F0.wireOp",EDGE,"E1");var subQ2=makeQuery(id+"F0.imprint","INTERSECT",VERTEX,{"disambiguationData":[OD(0.0)],"derivedFrom":[subQ1,subQ0]});Q12=makeQuery(id+"F0.imprint","IMPRINT",FACE,{"disambiguationData":[TD([[makeQuery(id+"F0.imprint","IMPRINT",EDGE,{"disambiguationData":[TD([[subQ2,1.0]])],"derivedFrom":subQ1}),1.0]])]});}
            var Q13;
            {var subQ0=sQuery(id+"F0.wireOp",EDGE,"E8");var subQ1=sQuery(id+"F0.wireOp",EDGE,"E1");var subQ2=makeQuery(id+"F0.imprint","INTERSECT",VERTEX,{"disambiguationData":[OD(1.0)],"derivedFrom":[subQ1,subQ0]});Q13=makeQuery(id+"F0.imprint","IMPRINT",FACE,{"disambiguationData":[TD([[makeQuery(id+"F0.imprint","IMPRINT",EDGE,{"disambiguationData":[TD([[subQ2,-1.0]])],"derivedFrom":subQ1}),1.0]])]});}
            var Q14;
            {var subQ0=sQuery(id+"F0.wireOp",EDGE,"E8");var subQ1=sQuery(id+"F0.wireOp",EDGE,"E1");var subQ2=makeQuery(id+"F0.imprint","INTERSECT",VERTEX,{"disambiguationData":[OD(1.0)],"derivedFrom":[subQ1,subQ0]});Q14=makeQuery(id+"F0.imprint","IMPRINT",FACE,{"disambiguationData":[TD([[makeQuery(id+"F0.imprint","IMPRINT",EDGE,{"disambiguationData":[TD([[subQ2,-1.0]])],"derivedFrom":subQ1}),-1.0]])]});}
            var Q15;
            {var subQ0=sQuery(id+"F0.wireOp",EDGE,"NZMgdJby-8j4q-fpOx-I2TN-UBzTeOVD87fY");var subQ1=sQuery(id+"F0.wireOp",EDGE,"E0");var subQ2=makeQuery(id+"F0.imprint","INTERSECT",VERTEX,{"disambiguationData":[OD(0.0)],"derivedFrom":[subQ1,subQ0]});Q15=makeQuery(id+"F0.imprint","IMPRINT",FACE,{"disambiguationData":[TD([[makeQuery(id+"F0.imprint","IMPRINT",EDGE,{"disambiguationData":[TD([[subQ2,1.0]])],"derivedFrom":subQ1}),-1.0]])]});}
            var Q16;
            {var subQ0=sQuery(id+"F0.wireOp",EDGE,"E9");var subQ1=sQuery(id+"F0.wireOp",EDGE,"E1");var subQ2=makeQuery(id+"F0.imprint","INTERSECT",VERTEX,{"disambiguationData":[OD(0.0)],"derivedFrom":[subQ1,subQ0]});Q16=makeQuery(id+"F0.imprint","IMPRINT",FACE,{"disambiguationData":[TD([[makeQuery(id+"F0.imprint","IMPRINT",EDGE,{"disambiguationData":[TD([[subQ2,-1.0]])],"derivedFrom":subQ1}),1.0]])]});}
            var Q17;
            {var subQ0=sQuery(id+"F0.wireOp",EDGE,"E9");var subQ1=sQuery(id+"F0.wireOp",EDGE,"E1");var subQ2=makeQuery(id+"F0.imprint","INTERSECT",VERTEX,{"disambiguationData":[OD(1.0)],"derivedFrom":[subQ1,subQ0]});Q17=makeQuery(id+"F0.imprint","IMPRINT",FACE,{"disambiguationData":[TD([[makeQuery(id+"F0.imprint","IMPRINT",EDGE,{"disambiguationData":[TD([[subQ2,1.0]])],"derivedFrom":subQ1}),1.0]])]});}
            var Q18;
            {var subQ0=sQuery(id+"F0.wireOp",EDGE,"E9");var subQ1=sQuery(id+"F0.wireOp",EDGE,"E1");var subQ2=makeQuery(id+"F0.imprint","INTERSECT",VERTEX,{"disambiguationData":[OD(0.0)],"derivedFrom":[subQ1,subQ0]});Q18=makeQuery(id+"F0.imprint","IMPRINT",FACE,{"disambiguationData":[TD([[makeQuery(id+"F0.imprint","IMPRINT",EDGE,{"disambiguationData":[TD([[subQ2,-1.0]])],"derivedFrom":subQ1}),-1.0]])]});}
            var Q19;
            {var subQ0=sQuery(id+"F0.wireOp",EDGE,"E9");var subQ1=sQuery(id+"F0.wireOp",EDGE,"E1");var subQ2=makeQuery(id+"F0.imprint","INTERSECT",VERTEX,{"disambiguationData":[OD(1.0)],"derivedFrom":[subQ1,subQ0]});Q19=makeQuery(id+"F0.imprint","IMPRINT",FACE,{"disambiguationData":[TD([[makeQuery(id+"F0.imprint","IMPRINT",EDGE,{"disambiguationData":[TD([[subQ2,1.0]])],"derivedFrom":subQ1}),-1.0]])]});}
            extrude(context, id + "F1", {"entities" : qUnion([Q0, Q1, Q2, Q3, Q4, Q5, Q6, Q7, Q8, Q9, Q10, Q11, Q12, Q13, Q14, Q15, Q16, Q17, Q18, Q19]), "depth" : 5 * mm});
        }
        {
            var Q0;
            Q0=makeQuery(id+"F0.imprint","IMPRINT",FACE,{"disambiguationData":[TD([[makeQuery(id+"F0.imprint","IMPRINT",EDGE,{"derivedFrom":sQuery(id+"F0.wireOp",EDGE,"E11")}),-1.0]])]});
            var Q1;
            {var subQ4=sQuery(id+"F0.wireOp",EDGE,"eX9GSUrg-MID6-gBVy-tWHq-VBg89v5eYroS");var subQ5=sQuery(id+"F0.wireOp",EDGE,"E12");var subQ6=makeQuery(id+"F0.imprint","INTERSECT",VERTEX,{"disambiguationData":[OD(0.0)],"derivedFrom":[subQ5,subQ4]});Q1=makeQuery(id+"F0.imprint","IMPRINT",FACE,{"disambiguationData":[TD([[makeQuery(id+"F0.imprint","IMPRINT",EDGE,{"disambiguationData":[TD([[subQ6,1.0]])],"derivedFrom":subQ5}),1.0]])]});}
            extrude(context, id + "F2", {"entities" : qUnion([Q0, Q1]), "depth" : 25 * mm});
        }
        {
            var Q0;
            Q0=makeQuery(id+"F0.imprint","IMPRINT",FACE,{"disambiguationData":[TD([[makeQuery(id+"F0.imprint","IMPRINT",EDGE,{"derivedFrom":sQuery(id+"F0.wireOp",EDGE,"E11")}),1.0]])]});
            extrude(context, id + "F3", {"entities" : qUnion([Q0]), "depth" : 35 * mm});
        }
    });
